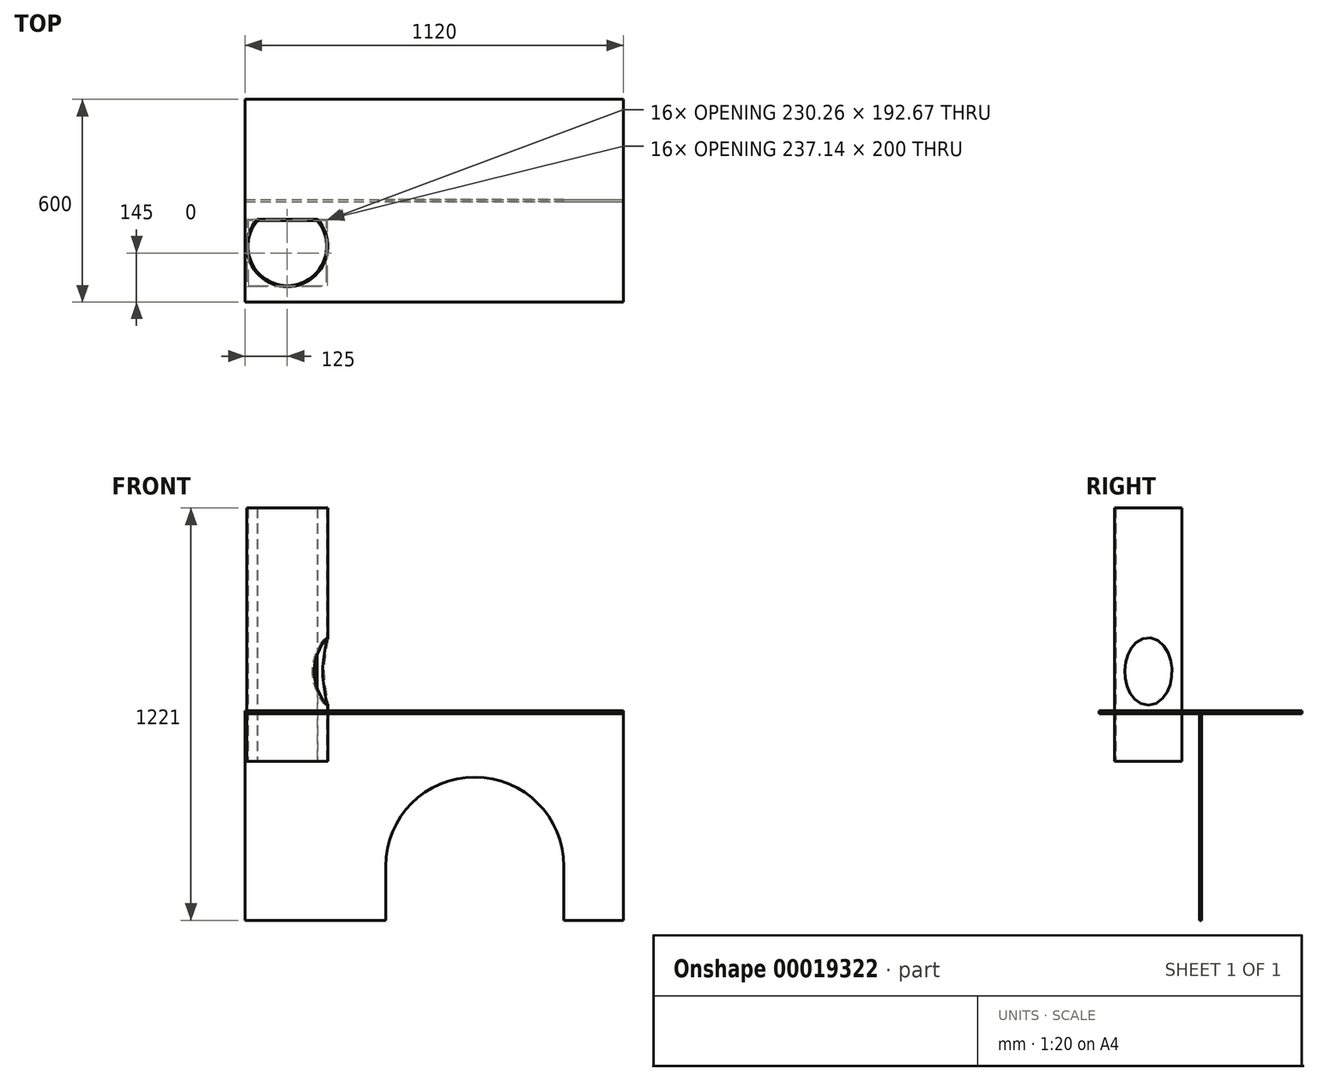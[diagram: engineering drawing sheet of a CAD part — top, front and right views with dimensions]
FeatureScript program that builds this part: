
annotation { "Feature Type Name" : "Feature", "Feature Type Description" : "" }
export const myFeature = defineFeature(function(context is Context, id is Id, definition is map)
    precondition{}
    {
        {
            var Q0;
            Q0=qCreatedBy(makeId("Top.planeOp"),FACE);
            var sketch = newSketch(context, id + "F0", { "sketchPlane" : qUnion([Q0])});
            skLineSegment(sketch, "E0.bottom", {"start": v(-560, 300) * mm, "end": v(560, 300) * mm});
            skLineSegment(sketch, "E0.top", {"start": v(-560, -300) * mm, "end": v(560, -300) * mm});
            skLineSegment(sketch, "E0.left", {"start": v(-560, 300) * mm, "end": v(-560, -300) * mm});
            skLineSegment(sketch, "E0.right", {"start": v(560, 300) * mm, "end": v(560, -300) * mm});
            skArc(sketch, "E1", {"start": v(-524.44, -55) * mm, "mid": v(-435, -255) * mm, "end": v(-345.56, -55) * mm});
            skLineSegment(sketch, "E2", {"start": v(-524.44, -55) * mm, "end": v(-345.56, -55) * mm});
            skSolve(sketch);
        }
        {
            var Q0;
            Q0=qSketchRegion(id+"F0",true);
            extrude(context, id + "F1", {"entities" : qUnion([Q0]), "depth" : 9 * mm});
        }
        {
            var Q0;
            Q0=qCreatedBy(makeId("Front.planeOp"),FACE);
            var sketch = newSketch(context, id + "F2", { "sketchPlane" : qUnion([Q0])});
            skLineSegment(sketch, "E3.bottom", {"start": v(-560, 0) * mm, "end": v(560, 0) * mm});
            skLineSegment(sketch, "E3.top", {"start": v(-560, -612) * mm, "end": v(560, -612) * mm});
            skLineSegment(sketch, "E3.left", {"start": v(-560, 0) * mm, "end": v(-560, -612) * mm});
            skLineSegment(sketch, "E3.right", {"start": v(560, 0) * mm, "end": v(560, -612) * mm});
            skSolve(sketch);
        }
        {
            var Q0;
            Q0=makeQuery(id+"F2.imprint","IMPRINT",FACE,{"disambiguationData":[TD([[makeQuery(id+"F2.imprint","IMPRINT",EDGE,{"derivedFrom":sQuery(id+"F2.wireOp",EDGE,"E3.bottom")}),-1.0]])]});
            extrude(context, id + "F3", {"entities" : qUnion([Q0]), "endBound" : BoundingType.SYMMETRIC, "depth" : 6 * mm});
        }
        {
            var Q0;
            Q0=makeQuery(id+"F1.opExtrude","CAP_FACE",FACE,{"disambiguationData":[OSD([sQuery(id+"F0.wireOp",EDGE,"E0.bottom"),sQuery(id+"F0.wireOp",EDGE,"E0.top"),sQuery(id+"F0.wireOp",EDGE,"E0.left"),sQuery(id+"F0.wireOp",EDGE,"E0.right"),sQuery(id+"F0.wireOp",EDGE,"E1")])],"isStart":false});
            var sketch = newSketch(context, id + "F4", { "sketchPlane" : qUnion([Q0])});
            skArc(sketch, "E4.0", {"start": v(-524.44, -55) * mm, "mid": v(-435, -255) * mm, "end": v(-345.56, -55) * mm});
            skLineSegment(sketch, "E4.1", {"start": v(-524.44, -55) * mm, "end": v(-345.56, -55) * mm});
            skLineSegment(sketch, "E5.0", {"start": v(-522.79, -58.66) * mm, "end": v(-347.21, -58.66) * mm});
            skArc(sketch, "E5.1", {"start": v(-522.79, -58.66) * mm, "mid": v(-435, -251.34) * mm, "end": v(-347.21, -58.66) * mm});
            skSolve(sketch);
        }
        {
            var Q0;
            {var subQ4=sQuery(id+"F4.wireOp",EDGE,"E4.0");Q0=makeQuery(id+"F4.imprint","IMPRINT",FACE,{"disambiguationData":[TD([[makeQuery(id+"F4.imprint","IMPRINT",EDGE,{"derivedFrom":subQ4}),1.0]])]});}
            extrude(context, id + "F5", {"entities" : qUnion([Q0]), "depth" : 600 * mm, "hasSecondDirection" : true, "secondDirectionOppositeDirection" : true, "secondDirectionDepth" : 150 * mm});
        }
        {
            var Q0;
            Q0=makeQuery(id+"F3.opExtrude","CAP_FACE",FACE,{"disambiguationData":[OSD([sQuery(id+"F2.wireOp",EDGE,"E3.bottom"),sQuery(id+"F2.wireOp",EDGE,"E3.top"),sQuery(id+"F2.wireOp",EDGE,"E3.left"),sQuery(id+"F2.wireOp",EDGE,"E3.right")])],"isStart":false});
            var sketch = newSketch(context, id + "F6", { "sketchPlane" : qUnion([Q0])});
            skLineSegment(sketch, "E6", {"start": v(380, -612) * mm, "end": v(380, -442) * mm, "construction": true});
            skLineSegment(sketch, "E7", {"start": v(380, -442) * mm, "end": v(305, -442) * mm, "construction": true});
            skLineSegment(sketch, "E8", {"start": v(305, -442) * mm, "end": v(305, -367) * mm, "construction": true});
            skLineSegment(sketch, "E9", {"start": v(305, -367) * mm, "end": v(230, -367) * mm, "construction": true});
            skLineSegment(sketch, "E10", {"start": v(230, -367) * mm, "end": v(230, -192) * mm, "construction": true});
            skLineSegment(sketch, "E11", {"start": v(230, -192) * mm, "end": v(10, -192) * mm, "construction": true});
            skLineSegment(sketch, "E12", {"start": v(10, -192) * mm, "end": v(10, -367) * mm, "construction": true});
            skLineSegment(sketch, "E13", {"start": v(10, -367) * mm, "end": v(-65, -367) * mm, "construction": true});
            skLineSegment(sketch, "E14", {"start": v(-65, -367) * mm, "end": v(-65, -442) * mm, "construction": true});
            skLineSegment(sketch, "E15", {"start": v(-65, -442) * mm, "end": v(-140, -442) * mm, "construction": true});
            skLineSegment(sketch, "E16", {"start": v(-140, -442) * mm, "end": v(-140, -612) * mm, "construction": true});
            skLineSegment(sketch, "E17", {"start": v(-140, -612) * mm, "end": v(380, -612) * mm, "construction": true});
            skLineSegment(sketch, "E18", {"start": v(-140, -192) * mm, "end": v(380, -192) * mm, "construction": true});
            skArc(sketch, "E19", {"start": v(380, -452) * mm, "mid": v(120, -192) * mm, "end": v(-140, -452) * mm, "construction": true});
            skLineSegment(sketch, "E20", {"start": v(-140, -452) * mm, "end": v(-140, -612) * mm, "construction": true});
            skLineSegment(sketch, "E21", {"start": v(380, -612) * mm, "end": v(380, -452) * mm, "construction": true});
            skLineSegment(sketch, "E22.0", {"start": v(-144, -616) * mm, "end": v(384, -616) * mm});
            skLineSegment(sketch, "E22.1", {"start": v(-144, -452) * mm, "end": v(-144, -616) * mm});
            skArc(sketch, "E22.2", {"start": v(384, -452) * mm, "mid": v(120, -188) * mm, "end": v(-144, -452) * mm});
            skLineSegment(sketch, "E22.3", {"start": v(384, -616) * mm, "end": v(384, -452) * mm});
            skSolve(sketch);
        }
        {
            var Q0;
            Q0=qSketchRegion(id+"F6",true);
            extrude(context, id + "F7", {"entities" : qUnion([Q0]), "operationType" : NewBodyOperationType.REMOVE, "oppositeDirection" : true, "depth" : 25 * mm});
        }
        {
            var Q0;
            Q0=qCreatedBy(makeId("Right.planeOp"),FACE);
            var sketch = newSketch(context, id + "F8", { "sketchPlane" : qUnion([Q0])});
            skEllipse(sketch, "E23", {"center": v(-155, 125) * mm, "majorRadius": 100 * mm, "minorRadius": 70 * mm, "majorAxis": v(0, -1)});
            skSolve(sketch);
        }
        {
            var Q0;
            Q0=qSketchRegion(id+"F8",true);
            extrude(context, id + "F9", {"entities" : qUnion([Q0]), "operationType" : NewBodyOperationType.REMOVE, "oppositeDirection" : true, "depth" : 384.63 * mm});
        }
    });
